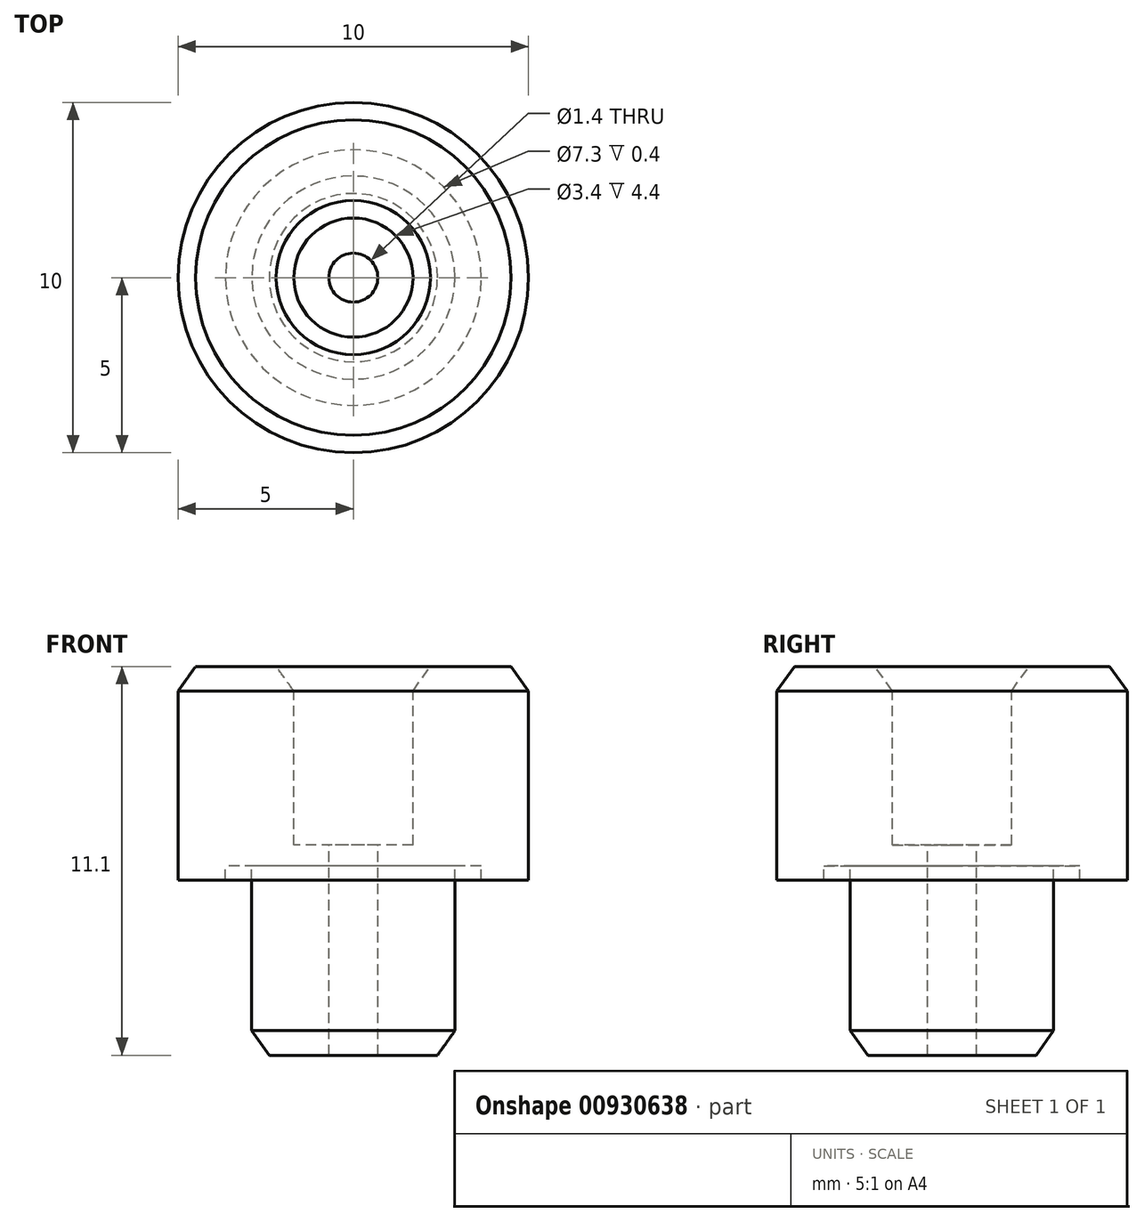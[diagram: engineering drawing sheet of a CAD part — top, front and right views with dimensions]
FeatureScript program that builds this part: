
annotation { "Feature Type Name" : "Feature", "Feature Type Description" : "" }
export const myFeature = defineFeature(function(context is Context, id is Id, definition is map)
    precondition{}
    {
        {
            var Q0;
            Q0=qCreatedBy(makeId("Front.planeOp"),FACE);
            var sketch = newSketch(context, id + "F0", { "sketchPlane" : qUnion([Q0])});
            skLineSegment(sketch, "E0", {"start": v(0.7, 0) * mm, "end": v(2.9, 0) * mm});
            skLineSegment(sketch, "E1", {"start": v(2.9, 0) * mm, "end": v(2.9, 5.4) * mm});
            skLineSegment(sketch, "E2", {"start": v(2.9, 5.4) * mm, "end": v(3.65, 5.4) * mm});
            skLineSegment(sketch, "E3", {"start": v(3.65, 5.4) * mm, "end": v(3.65, 5) * mm});
            skLineSegment(sketch, "E4", {"start": v(3.65, 5) * mm, "end": v(5, 5) * mm});
            skLineSegment(sketch, "E5", {"start": v(5, 5) * mm, "end": v(5, 11.1) * mm});
            skLineSegment(sketch, "E6", {"start": v(5, 11.1) * mm, "end": v(1.7, 11.1) * mm});
            skLineSegment(sketch, "E7", {"start": v(1.7, 11.1) * mm, "end": v(1.7, 6) * mm});
            skLineSegment(sketch, "E8", {"start": v(1.7, 6) * mm, "end": v(0.7, 6) * mm});
            skLineSegment(sketch, "E9", {"start": v(0.7, 6) * mm, "end": v(0.7, 0) * mm});
            skLineSegment(sketch, "E10", {"start": v(0, 11.1) * mm, "end": v(0, 0) * mm, "construction": true});
            skSolve(sketch);
        }
        {
            var Q0;
            Q0=qSketchRegion(id+"F0",true);
            var Q1;
            Q1=sQuery(id+"F0.wireOp",EDGE,"E10");
            revolve(context, id + "F1", {"surfaceOperationType" : NewSurfaceOperationType.NEW, "entities" : qUnion([Q0]), "axis" : qUnion([Q1]), "revolveType" : RevolveType.FULL});
        }
        {
            var Q0;
            Q0=makeQuery(id+"F1.opRevolve","SWEPT_EDGE",EDGE,{"disambiguationData":[OSD([sQuery(id+"F0.wireOp",EDGE,"E6"),sQuery(id+"F0.wireOp",EDGE,"E7")])]});
            var Q1;
            Q1=makeQuery(id+"F1.opRevolve","SWEPT_EDGE",EDGE,{"disambiguationData":[OSD([sQuery(id+"F0.wireOp",EDGE,"E0"),sQuery(id+"F0.wireOp",EDGE,"E1")])]});
            var Q2;
            Q2=makeQuery(id+"F1.opRevolve","SWEPT_EDGE",EDGE,{"disambiguationData":[OSD([sQuery(id+"F0.wireOp",EDGE,"E5"),sQuery(id+"F0.wireOp",EDGE,"E6")])]});
            chamfer(context, id + "F2", {"entities" : qUnion([Q0, Q1, Q2]), "chamferType" : ChamferType.TWO_OFFSETS, "width1" : 0.7 * mm, "oppositeDirection" : false, "width2" : 0.5 * mm, "tangentPropagation" : true});
        }
    });
